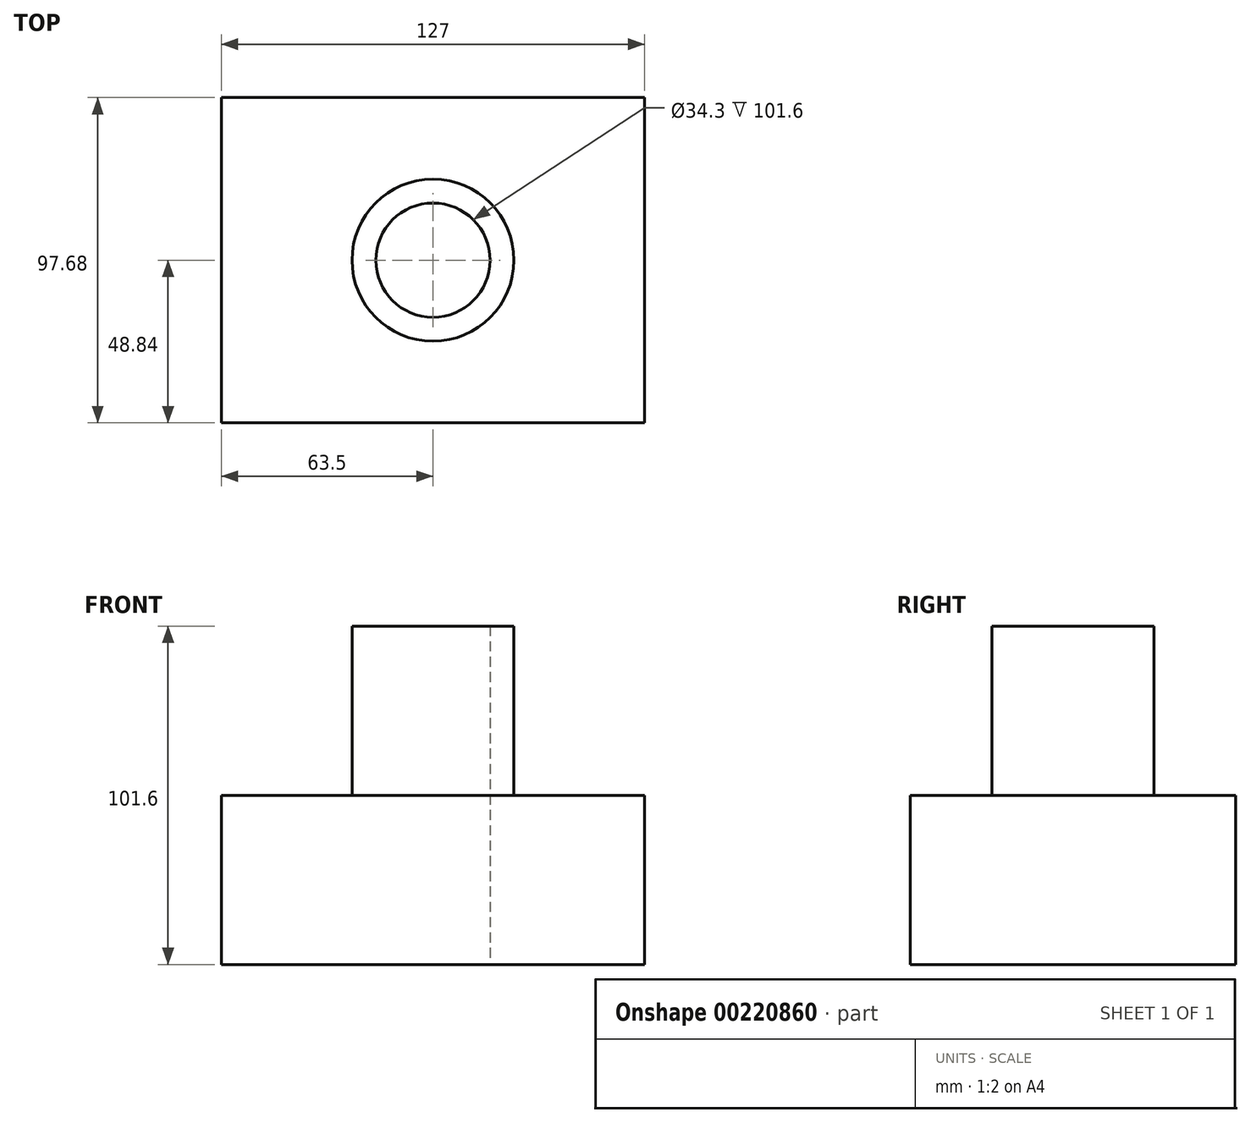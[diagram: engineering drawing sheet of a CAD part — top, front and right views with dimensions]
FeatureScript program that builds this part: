
annotation { "Feature Type Name" : "Feature", "Feature Type Description" : "" }
export const myFeature = defineFeature(function(context is Context, id is Id, definition is map)
    precondition{}
    {
        {
            var Q0;
            Q0=qCreatedBy(makeId("Top.planeOp"),FACE);
            var sketch = newSketch(context, id + "F0", { "sketchPlane" : qUnion([Q0])});
            skLineSegment(sketch, "E0.bottom", {"start": v(-63.5, 48.84) * mm, "end": v(63.5, 48.84) * mm});
            skLineSegment(sketch, "E0.top", {"start": v(-63.5, -48.84) * mm, "end": v(63.5, -48.84) * mm});
            skLineSegment(sketch, "E0.left", {"start": v(-63.5, 48.84) * mm, "end": v(-63.5, -48.84) * mm});
            skLineSegment(sketch, "E0.right", {"start": v(63.5, 48.84) * mm, "end": v(63.5, -48.84) * mm});
            skPoint(sketch, "E0.middle", {"position": v(0, 0) * mm});
            skCircle(sketch, "E1", {"center": v(0, 0) * mm, "radius": 17.15 * mm});
            skCircle(sketch, "E2", {"center": v(0, 0) * mm, "radius": 24.3 * mm});
            skSolve(sketch);
        }
        {
            var Q0;
            Q0=makeQuery(id+"F0.imprint","IMPRINT",FACE,{"disambiguationData":[TD([[makeQuery(id+"F0.imprint","IMPRINT",EDGE,{"derivedFrom":sQuery(id+"F0.wireOp",EDGE,"E0.bottom")}),-1.0]])]});
            var Q1;
            Q1=makeQuery(id+"F0.imprint","IMPRINT",FACE,{"disambiguationData":[TD([[makeQuery(id+"F0.imprint","IMPRINT",EDGE,{"derivedFrom":sQuery(id+"F0.wireOp",EDGE,"E1")}),-1.0]])]});
            extrude(context, id + "F1", {"entities" : qUnion([Q0, Q1]), "depth" : 25.4 * mm});
        }
        {
            var Q0;
            Q0 = qSketchRegion(id + "F0", true);
            extrude(context, id + "F2", {"entities" : qUnion([Q0]), "operationType" : NewBodyOperationType.ADD, "depth" : 50.8 * mm});
        }
        {
            var Q0;
            Q0=makeQuery(id+"F1.opExtrude","CAP_FACE",FACE,{"disambiguationData":[OSD([sQuery(id+"F0.wireOp",EDGE,"E0.bottom"),sQuery(id+"F0.wireOp",EDGE,"E0.top"),sQuery(id+"F0.wireOp",EDGE,"E0.left"),sQuery(id+"F0.wireOp",EDGE,"E0.right"),sQuery(id+"F0.wireOp",EDGE,"E1")])],"isStart":false});
            extrude(context, id + "F3", {"entities" : qUnion([Q0]), "operationType" : NewBodyOperationType.ADD, "depth" : 76.2 * mm});
        }
    });
